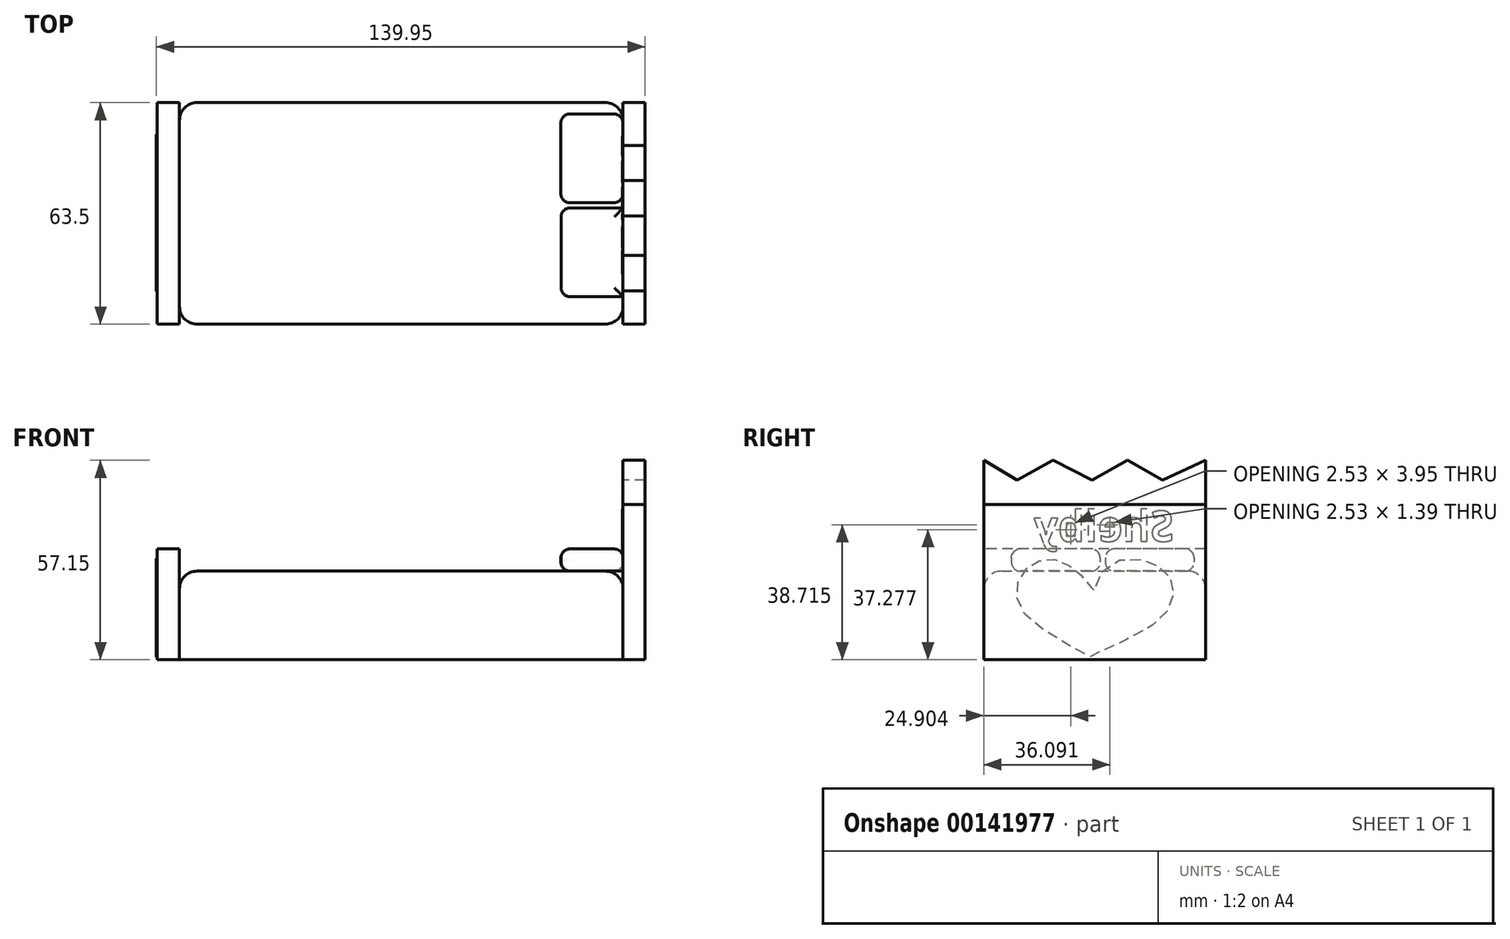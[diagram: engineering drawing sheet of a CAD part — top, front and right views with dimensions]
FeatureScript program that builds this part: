
annotation { "Feature Type Name" : "Feature", "Feature Type Description" : "" }
export const myFeature = defineFeature(function(context is Context, id is Id, definition is map)
    precondition{}
    {
        {
            var Q0;
            Q0=qCreatedBy(makeId("Front.planeOp"),FACE);
            var sketch = newSketch(context, id + "F0", { "sketchPlane" : qUnion([Q0])});
            skLineSegment(sketch, "E0.bottom", {"start": v(-63.5, 12.7) * mm, "end": v(63.5, 12.7) * mm});
            skLineSegment(sketch, "E0.top", {"start": v(-63.5, -12.7) * mm, "end": v(63.5, -12.7) * mm});
            skLineSegment(sketch, "E0.left", {"start": v(-63.5, 12.7) * mm, "end": v(-63.5, -12.7) * mm});
            skLineSegment(sketch, "E0.right", {"start": v(63.5, 12.7) * mm, "end": v(63.5, -12.7) * mm});
            skPoint(sketch, "E0.middle", {"position": v(0, 0) * mm});
            skSolve(sketch);
        }
        {
            var Q0;
            Q0 = qSketchRegion(id + "F0", true);
            extrude(context, id + "F1", {"entities" : qUnion([Q0]), "depth" : 63.5 * mm});
        }
        {
            var Q0;
            Q0=makeQuery(id+"F1.opExtrude","CAP_EDGE",EDGE,{"disambiguationData":[OSD([sQuery(id+"F0.wireOp",EDGE,"E0.bottom")])],"isStart":false});
            var Q1;
            Q1=makeQuery(id+"F1.opExtrude","CAP_EDGE",EDGE,{"disambiguationData":[OSD([sQuery(id+"F0.wireOp",EDGE,"E0.bottom")])],"isStart":true});
            fillet(context, id + "F2", {"entities" : qUnion([Q0, Q1]), "radius" : 5.08 * mm, "tangentPropagation" : true, "allowEdgeOverflow" : false});
        }
        {
            var Q0;
            Q0=makeQuery(id+"F1.opExtrude","CAP_EDGE",EDGE,{"disambiguationData":[OSD([sQuery(id+"F0.wireOp",EDGE,"E0.left")])],"isStart":false});
            var Q1;
            Q1=makeQuery(id+"F1.opExtrude","CAP_EDGE",EDGE,{"disambiguationData":[OSD([sQuery(id+"F0.wireOp",EDGE,"E0.right")])],"isStart":false});
            var Q2;
            Q2=makeQuery(id+"F1.opExtrude","CAP_EDGE",EDGE,{"disambiguationData":[OSD([sQuery(id+"F0.wireOp",EDGE,"E0.left")])],"isStart":true});
            var Q3;
            Q3=makeQuery(id+"F1.opExtrude","CAP_EDGE",EDGE,{"disambiguationData":[OSD([sQuery(id+"F0.wireOp",EDGE,"E0.right")])],"isStart":true});
            fillet(context, id + "F3", {"entities" : qUnion([Q0, Q1, Q2, Q3]), "radius" : 5.08 * mm, "tangentPropagation" : true, "allowEdgeOverflow" : false});
        }
        {
            var Q0;
            Q0=makeQuery(id+"F1.opExtrude","SWEPT_FACE",FACE,{"disambiguationData":[OSD([sQuery(id+"F0.wireOp",EDGE,"E0.left")])]});
            var sketch = newSketch(context, id + "F4", { "sketchPlane" : qUnion([Q0])});
            skLineSegment(sketch, "E1.bottom", {"start": v(0, -12.7) * mm, "end": v(63.5, -12.7) * mm});
            skLineSegment(sketch, "E1.top", {"start": v(0, 19.05) * mm, "end": v(63.5, 19.05) * mm});
            skLineSegment(sketch, "E1.left", {"start": v(0, -12.7) * mm, "end": v(0, 19.05) * mm});
            skLineSegment(sketch, "E1.right", {"start": v(63.5, -12.7) * mm, "end": v(63.5, 19.05) * mm});
            skSolve(sketch);
        }
        {
            var Q0;
            Q0 = qSketchRegion(id + "F4", true);
            extrude(context, id + "F5", {"entities" : qUnion([Q0]), "depth" : 6.35 * mm});
        }
        {
            var Q0;
            Q0=makeQuery(id+"F1.opExtrude","SWEPT_FACE",FACE,{"disambiguationData":[OSD([sQuery(id+"F0.wireOp",EDGE,"E0.right")])]});
            var sketch = newSketch(context, id + "F6", { "sketchPlane" : qUnion([Q0])});
            skLineSegment(sketch, "E2.bottom", {"start": v(0, -12.7) * mm, "end": v(-63.5, -12.7) * mm});
            skLineSegment(sketch, "E2.top", {"start": v(0, 31.75) * mm, "end": v(-63.5, 31.75) * mm});
            skLineSegment(sketch, "E2.left", {"start": v(0, -12.7) * mm, "end": v(0, 31.75) * mm});
            skLineSegment(sketch, "E2.right", {"start": v(-63.5, -12.7) * mm, "end": v(-63.5, 31.75) * mm});
            skSolve(sketch);
        }
        {
            var Q0;
            Q0 = qSketchRegion(id + "F6", true);
            extrude(context, id + "F7", {"entities" : qUnion([Q0]), "depth" : 6.35 * mm});
        }
        {
            var Q0;
            Q0=makeQuery(id+"F7.opExtrude","SWEPT_FACE",FACE,{"disambiguationData":[OSD([sQuery(id+"F6.wireOp",EDGE,"E2.top")])]});
            var sketch = newSketch(context, id + "F8", { "sketchPlane" : qUnion([Q0])});
            skLineSegment(sketch, "E3.bottom", {"start": v(63.5, -63.5) * mm, "end": v(69.85, -63.5) * mm});
            skLineSegment(sketch, "E3.top", {"start": v(63.5, 0) * mm, "end": v(69.85, 0) * mm});
            skLineSegment(sketch, "E3.left", {"start": v(63.5, -63.5) * mm, "end": v(63.5, 0) * mm});
            skLineSegment(sketch, "E3.right", {"start": v(69.85, -63.5) * mm, "end": v(69.85, 0) * mm});
            skSolve(sketch);
        }
        {
            var Q0;
            Q0 = qSketchRegion(id + "F8", true);
            extrude(context, id + "F9", {"entities" : qUnion([Q0]), "depth" : 12.7 * mm});
        }
        {
            var Q0;
            Q0=makeQuery(id+"F9.opExtrude","SWEPT_FACE",FACE,{"disambiguationData":[OSD([sQuery(id+"F8.wireOp",EDGE,"E3.left")])]});
            var sketch = newSketch(context, id + "F10", { "sketchPlane" : qUnion([Q0])});
            skLineSegment(sketch, "E4", {"start": v(0, 44.45) * mm, "end": v(12.3, 38.84) * mm});
            skLineSegment(sketch, "E5", {"start": v(12.3, 38.84) * mm, "end": v(22.28, 44.45) * mm});
            skLineSegment(sketch, "E6", {"start": v(22.28, 44.45) * mm, "end": v(32.47, 38.84) * mm});
            skLineSegment(sketch, "E7", {"start": v(32.47, 38.84) * mm, "end": v(43.72, 44.45) * mm});
            skLineSegment(sketch, "E8", {"start": v(43.72, 44.45) * mm, "end": v(53.9, 38.84) * mm});
            skLineSegment(sketch, "E9", {"start": v(53.9, 38.84) * mm, "end": v(63.5, 44.45) * mm});
            skLineSegment(sketch, "E10", {"start": v(63.5, 44.45) * mm, "end": v(0, 44.45) * mm});
            skSolve(sketch);
        }
        {
            var Q0;
            Q0 = qSketchRegion(id + "F10", true);
            extrude(context, id + "F11", {"entities" : qUnion([Q0]), "operationType" : NewBodyOperationType.REMOVE, "oppositeDirection" : true, "depth" : 25.4 * mm});
        }
        {
            var Q0;
            Q0=makeQuery(id+"F7.opExtrude","CAP_FACE",FACE,{"disambiguationData":[OSD([sQuery(id+"F6.wireOp",EDGE,"E2.bottom"),sQuery(id+"F6.wireOp",EDGE,"E2.top"),sQuery(id+"F6.wireOp",EDGE,"E2.left"),sQuery(id+"F6.wireOp",EDGE,"E2.right")])],"isStart":true});
            var sketch = newSketch(context, id + "F12", { "sketchPlane" : qUnion([Q0])});
            skText(sketch, "E11", { "text": "Shelby", "fontName": "OpenSans-Bold.ttf"});
            const initialGuessF12  = {"E11": [0.0091, 0.02126, 1, 0, 0.00872]};
            skSetInitialGuess(sketch, initialGuessF12);
            skSolve(sketch);
        }
        {
            var Q0;
            Q0 = qSketchRegion(id + "F12", true);
            extrude(context, id + "F13", {"entities" : qUnion([Q0]), "depth" : 0.13 * mm});
        }
        {
            var Q0;
            Q0=makeQuery(id+"F1.opExtrude","SWEPT_FACE",FACE,{"disambiguationData":[OSD([sQuery(id+"F0.wireOp",EDGE,"E0.bottom")])]});
            var sketch = newSketch(context, id + "F14", { "sketchPlane" : qUnion([Q0])});
            skLineSegment(sketch, "E12.bottom", {"start": v(63.5, -3.28) * mm, "end": v(45.71, -3.28) * mm});
            skLineSegment(sketch, "E12.top", {"start": v(63.5, -28.68) * mm, "end": v(45.71, -28.68) * mm});
            skLineSegment(sketch, "E12.left", {"start": v(63.5, -3.28) * mm, "end": v(63.5, -28.68) * mm});
            skLineSegment(sketch, "E12.right", {"start": v(45.71, -3.28) * mm, "end": v(45.71, -28.68) * mm});
            skLineSegment(sketch, "E13.bottom", {"start": v(45.76, -30.2) * mm, "end": v(63.54, -30.2) * mm});
            skLineSegment(sketch, "E13.top", {"start": v(45.76, -55.6) * mm, "end": v(63.54, -55.6) * mm});
            skLineSegment(sketch, "E13.left", {"start": v(45.76, -30.2) * mm, "end": v(45.76, -55.6) * mm});
            skLineSegment(sketch, "E13.right", {"start": v(63.54, -30.2) * mm, "end": v(63.54, -55.6) * mm});
            skSolve(sketch);
        }
        {
            var Q0;
            Q0 = qSketchRegion(id + "F14", true);
            extrude(context, id + "F15", {"entities" : qUnion([Q0]), "depth" : 6.35 * mm});
        }
        {
            var Q0;
            Q0=makeQuery(id+"F15.opExtrude","CAP_EDGE",EDGE,{"disambiguationData":[OSD([sQuery(id+"F14.wireOp",EDGE,"E12.right")])],"isStart":false});
            fillet(context, id + "F16", {"entities" : qUnion([Q0]), "radius" : 2.54 * mm, "tangentPropagation" : true, "allowEdgeOverflow" : false});
        }
        {
            var Q0;
            Q0=makeQuery(id+"F15.opExtrude","CAP_EDGE",EDGE,{"disambiguationData":[OSD([sQuery(id+"F14.wireOp",EDGE,"E12.top")])],"isStart":false});
            var Q1;
            Q1=makeQuery(id+"F15.opExtrude","CAP_EDGE",EDGE,{"disambiguationData":[OSD([sQuery(id+"F14.wireOp",EDGE,"E12.left")])],"isStart":false});
            var Q2;
            Q2=makeQuery(id+"F15.opExtrude","CAP_EDGE",EDGE,{"disambiguationData":[OSD([sQuery(id+"F14.wireOp",EDGE,"E12.bottom")])],"isStart":false});
            var Q3;
            Q3=makeQuery(id+"F15.opExtrude","CAP_EDGE",EDGE,{"disambiguationData":[OSD([sQuery(id+"F14.wireOp",EDGE,"E12.right")])],"isStart":true});
            var Q4;
            Q4=makeQuery(id+"F15.opExtrude","SWEPT_EDGE",EDGE,{"disambiguationData":[OSD([sQuery(id+"F14.wireOp",EDGE,"E12.top"),sQuery(id+"F14.wireOp",EDGE,"E12.right")])]});
            fillet(context, id + "F17", {"entities" : qUnion([Q0, Q1, Q2, Q3, Q4]), "radius" : 2.54 * mm, "tangentPropagation" : true, "allowEdgeOverflow" : false});
        }
        {
            var Q0;
            Q0=makeQuery(id+"F15.opExtrude","SWEPT_EDGE",EDGE,{"disambiguationData":[OSD([sQuery(id+"F14.wireOp",EDGE,"E12.bottom"),sQuery(id+"F14.wireOp",EDGE,"E12.left")])]});
            var Q1;
            Q1=makeQuery(id+"F15.opExtrude","CAP_EDGE",EDGE,{"disambiguationData":[OSD([sQuery(id+"F14.wireOp",EDGE,"E12.bottom")])],"isStart":true});
            var Q2;
            Q2=makeQuery(id+"F15.opExtrude","CAP_EDGE",EDGE,{"disambiguationData":[OSD([sQuery(id+"F14.wireOp",EDGE,"E13.bottom")])],"isStart":false});
            var Q3;
            Q3=makeQuery(id+"F15.opExtrude","CAP_EDGE",EDGE,{"disambiguationData":[OSD([sQuery(id+"F14.wireOp",EDGE,"E13.left")])],"isStart":false});
            var Q4;
            Q4=makeQuery(id+"F15.opExtrude","CAP_EDGE",EDGE,{"disambiguationData":[OSD([sQuery(id+"F14.wireOp",EDGE,"E13.top")])],"isStart":false});
            var Q5;
            Q5=makeQuery(id+"F15.opExtrude","CAP_EDGE",EDGE,{"disambiguationData":[OSD([sQuery(id+"F14.wireOp",EDGE,"E13.right")])],"isStart":false});
            var Q6;
            Q6=makeQuery(id+"F15.opExtrude","SWEPT_EDGE",EDGE,{"disambiguationData":[OSD([sQuery(id+"F14.wireOp",EDGE,"E13.bottom"),sQuery(id+"F14.wireOp",EDGE,"E13.left")])]});
            var Q7;
            Q7=makeQuery(id+"F15.opExtrude","CAP_EDGE",EDGE,{"disambiguationData":[OSD([sQuery(id+"F14.wireOp",EDGE,"E13.left")])],"isStart":true});
            var Q8;
            Q8=makeQuery(id+"F15.opExtrude","CAP_EDGE",EDGE,{"disambiguationData":[OSD([sQuery(id+"F14.wireOp",EDGE,"E13.top")])],"isStart":true});
            var Q9;
            Q9=makeQuery(id+"F15.opExtrude","SWEPT_EDGE",EDGE,{"disambiguationData":[OSD([sQuery(id+"F14.wireOp",EDGE,"E13.top"),sQuery(id+"F14.wireOp",EDGE,"E13.left")])]});
            fillet(context, id + "F18", {"entities" : qUnion([Q0, Q1, Q2, Q3, Q4, Q5, Q6, Q7, Q8, Q9]), "radius" : 2.54 * mm, "tangentPropagation" : true, "allowEdgeOverflow" : false});
        }
        {
            var Q0;
            {var subQ0=sQuery(id+"F14.wireOp",EDGE,"E13.left");Q0=makeQuery(id+"F18.opFillet","BLEND_EDGE",EDGE,{"blendedFrom":[makeQuery(id+"F15.opExtrude","SWEPT_EDGE",EDGE,{"disambiguationData":[OSD([sQuery(id+"F14.wireOp",EDGE,"E13.bottom"),subQ0])]}),makeQuery(id+"F15.opExtrude","CAP_EDGE",EDGE,{"disambiguationData":[OSD([subQ0])],"isStart":true})],"blendedInto":[]});}
            fillet(context, id + "F19", {"entities" : qUnion([Q0]), "radius" : 2.54 * mm, "tangentPropagation" : true, "allowEdgeOverflow" : false});
        }
        {
            var Q0;
            {var subQ0=sQuery(id+"F14.wireOp",EDGE,"E12.right");Q0=makeQuery(id+"F17.opFillet","BLEND_EDGE",EDGE,{"blendedFrom":[makeQuery(id+"F15.opExtrude","CAP_EDGE",EDGE,{"disambiguationData":[OSD([subQ0])],"isStart":true}),makeQuery(id+"F15.opExtrude","SWEPT_EDGE",EDGE,{"disambiguationData":[OSD([sQuery(id+"F14.wireOp",EDGE,"E12.top"),subQ0])]})],"blendedInto":[]});}
            fillet(context, id + "F20", {"entities" : qUnion([Q0]), "radius" : 2.54 * mm, "tangentPropagation" : true, "allowEdgeOverflow" : false});
        }
        {
            var Q0;
            {var subQ0=sQuery(id+"F14.wireOp",EDGE,"E12.bottom");Q0=makeQuery(id+"F18.opFillet","BLEND_EDGE",EDGE,{"blendedFrom":[makeQuery(id+"F15.opExtrude","SWEPT_EDGE",EDGE,{"disambiguationData":[OSD([subQ0,sQuery(id+"F14.wireOp",EDGE,"E12.left")])]}),makeQuery(id+"F15.opExtrude","CAP_EDGE",EDGE,{"disambiguationData":[OSD([subQ0])],"isStart":true})],"blendedInto":[]});}
            fillet(context, id + "F21", {"entities" : qUnion([Q0]), "radius" : 2.54 * mm, "tangentPropagation" : true, "allowEdgeOverflow" : false});
        }
        {
            var Q0;
            Q0=makeQuery(id+"F5.opExtrude","CAP_FACE",FACE,{"disambiguationData":[OSD([sQuery(id+"F4.wireOp",EDGE,"E1.bottom"),sQuery(id+"F4.wireOp",EDGE,"E1.top"),sQuery(id+"F4.wireOp",EDGE,"E1.left"),sQuery(id+"F4.wireOp",EDGE,"E1.right")])],"isStart":false});
            var sketch = newSketch(context, id + "F22", { "sketchPlane" : qUnion([Q0])});
            skFitSpline(sketch, "E14", {"points": [v(29.76, 12.53) * mm, v(20.6, 16.27) * mm, v(12.8, 13.65) * mm, v(9.39, 8.95) * mm, v(10.42, 2.19) * mm, v(19.02, -5.14) * mm, v(32.39, -11.74) * mm, v(32.47, -11.9) * mm, v(45.68, -4.58) * mm, v(53.24, 2.74) * mm, v(53.87, 8.87) * mm, v(50.85, 13.8) * mm, v(46.47, 15.95) * mm, v(41.22, 15.56) * mm, v(36.6, 12.37) * mm, v(32.86, 8.16) * mm, v(32.15, 6.48) * mm, v(29.76, 12.53) * mm]});
            skSolve(sketch);
        }
        {
            var Q0;
            Q0 = qSketchRegion(id + "F22", true);
            extrude(context, id + "F23", {"entities" : qUnion([Q0]), "depth" : 0.25 * mm});
        }
    });
